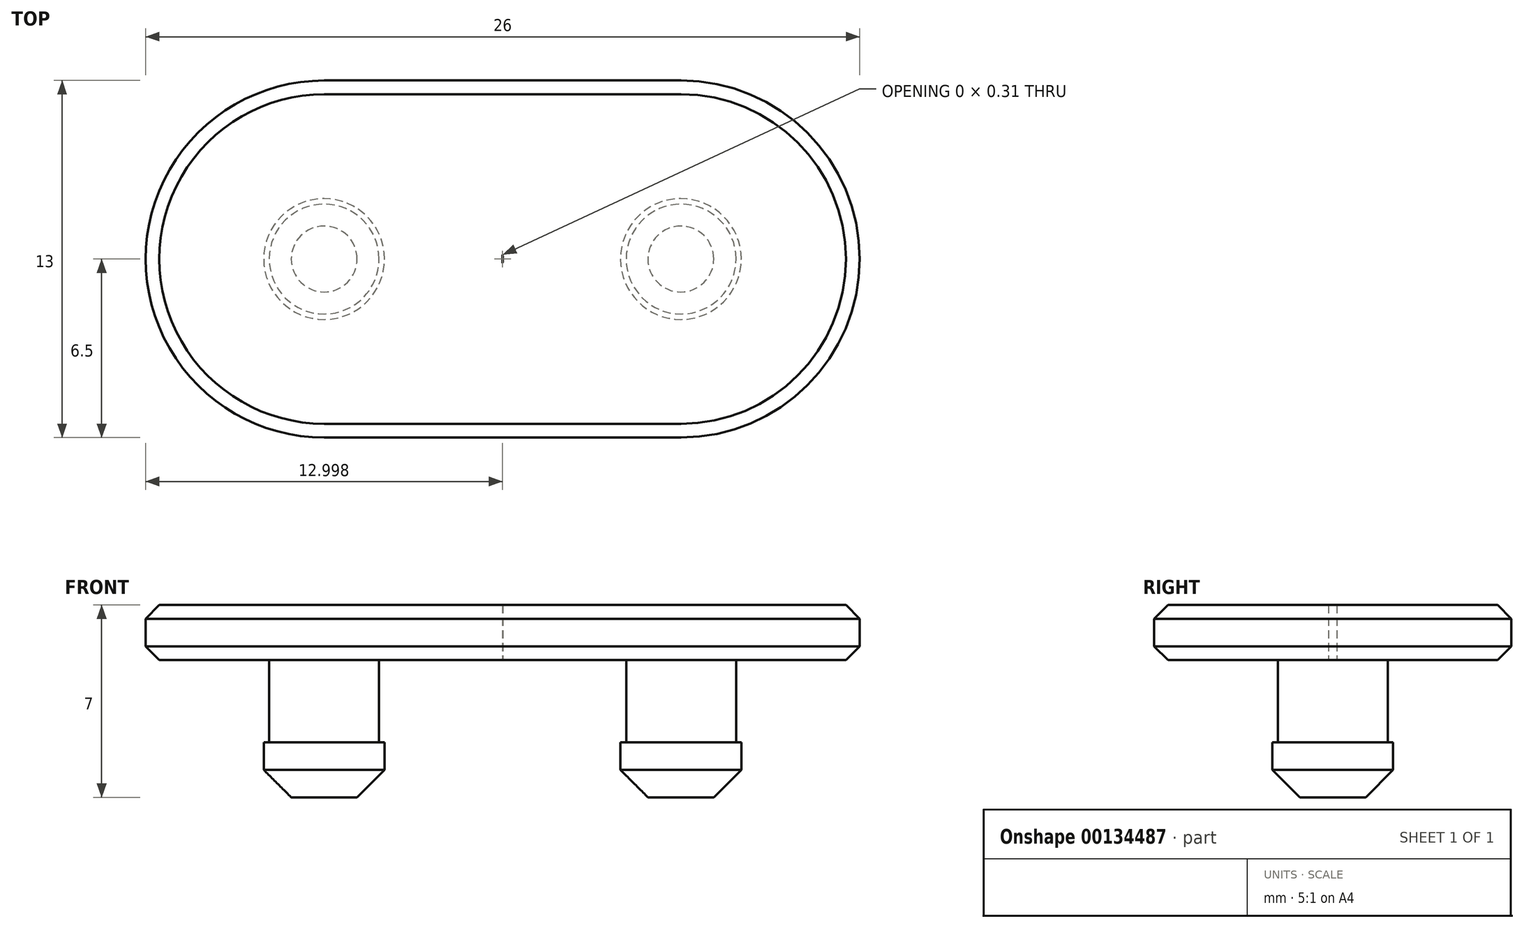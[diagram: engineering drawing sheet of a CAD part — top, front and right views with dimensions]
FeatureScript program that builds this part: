
annotation { "Feature Type Name" : "Feature", "Feature Type Description" : "" }
export const myFeature = defineFeature(function(context is Context, id is Id, definition is map)
    precondition{}
    {
        {
            var Q0;
            Q0=qCreatedBy(makeId("Top.planeOp"),FACE);
            var sketch = newSketch(context, id + "F0", { "sketchPlane" : qUnion([Q0])});
            skLineSegment(sketch, "E0.bottom", {"start": v(6.5, -6.5) * mm, "end": v(-6.5, -6.5) * mm});
            skLineSegment(sketch, "E0.top", {"start": v(6.5, 6.5) * mm, "end": v(-6.5, 6.5) * mm});
            skLineSegment(sketch, "E0.left", {"start": v(13, -0.3) * mm, "end": v(13, 0.3) * mm});
            skLineSegment(sketch, "E0.right", {"start": v(-13, -0.3) * mm, "end": v(-13, 0.3) * mm});
            skPoint(sketch, "E0.middle", {"position": v(0, 0) * mm});
            skPoint(sketch, "E1.visualSharp", {"position": v(-13, 6.5) * mm});
            skPoint(sketch, "E2.visualSharp", {"position": v(-13, -6.5) * mm});
            skPoint(sketch, "E3.visualSharp", {"position": v(13, 6.5) * mm});
            skPoint(sketch, "E4.visualSharp", {"position": v(13, -6.5) * mm});
            skLineSegment(sketch, "E5", {"start": v(0, 6.5) * mm, "end": v(0, -6.5) * mm, "construction": true});
            skLineSegment(sketch, "E6", {"start": v(0, 0) * mm, "end": v(13, 0) * mm, "construction": true});
            skCircle(sketch, "E7", {"center": v(6.5, 0) * mm, "radius": 2 * mm});
            skLineSegment(sketch, "E8", {"start": v(-13, 0) * mm, "end": v(0, 0) * mm, "construction": true});
            skCircle(sketch, "E9", {"center": v(-6.5, 0) * mm, "radius": 2 * mm});
            skCircle(sketch, "E10", {"center": v(-6.5, 0) * mm, "radius": 6.5 * mm});
            skCircle(sketch, "E11", {"center": v(6.5, 0) * mm, "radius": 6.5 * mm});
            skSolve(sketch);
        }
        {
            var Q0;
            Q0 = qSketchRegion(id + "F0", true);
            var Q1;
            Q1=makeQuery(id+"F0.imprint","IMPRINT",FACE,{"disambiguationData":[TD([[makeQuery(id+"F0.imprint","IMPRINT",EDGE,{"derivedFrom":sQuery(id+"F0.wireOp",EDGE,"E9")}),1.0]])]});
            var Q2;
            Q2=makeQuery(id+"F0.imprint","IMPRINT",FACE,{"disambiguationData":[TD([[makeQuery(id+"F0.imprint","IMPRINT",EDGE,{"derivedFrom":sQuery(id+"F0.wireOp",EDGE,"E7")}),1.0]])]});
            extrude(context, id + "F1", {"entities" : qUnion([Q0, Q1, Q2]), "depth" : 2 * mm});
        }
        {
            var Q0;
            Q0=makeQuery(id+"F0.imprint","IMPRINT",FACE,{"disambiguationData":[TD([[makeQuery(id+"F0.imprint","IMPRINT",EDGE,{"derivedFrom":sQuery(id+"F0.wireOp",EDGE,"E9")}),1.0]])]});
            var Q1;
            Q1=makeQuery(id+"F0.imprint","IMPRINT",FACE,{"disambiguationData":[TD([[makeQuery(id+"F0.imprint","IMPRINT",EDGE,{"derivedFrom":sQuery(id+"F0.wireOp",EDGE,"E7")}),1.0]])]});
            extrude(context, id + "F2", {"entities" : qUnion([Q0, Q1]), "operationType" : NewBodyOperationType.ADD, "oppositeDirection" : true, "depth" : 3 * mm});
        }
        {
            var Q0;
            Q0=makeQuery(id+"F2.opExtrude","CAP_FACE",FACE,{"disambiguationData":[OSD([sQuery(id+"F0.wireOp",EDGE,"E9")])],"isStart":false});
            var sketch = newSketch(context, id + "F3", { "sketchPlane" : qUnion([Q0])});
            skCircle(sketch, "E12", {"center": v(-6.5, 0) * mm, "radius": 2.2 * mm});
            skCircle(sketch, "E13", {"center": v(6.49, 0) * mm, "radius": 2.2 * mm});
            skSolve(sketch);
        }
        {
            var Q0;
            Q0 = qSketchRegion(id + "F3", true);
            extrude(context, id + "F4", {"entities" : qUnion([Q0]), "operationType" : NewBodyOperationType.ADD, "depth" : 2 * mm});
        }
        {
            var Q0;
            Q0=makeQuery(id+"F4.opExtrude","CAP_EDGE",EDGE,{"disambiguationData":[OSD([sQuery(id+"F3.wireOp",EDGE,"E12")])],"isStart":false});
            var Q1;
            Q1=makeQuery(id+"F4.opExtrude","CAP_EDGE",EDGE,{"disambiguationData":[OSD([sQuery(id+"F3.wireOp",EDGE,"E13")])],"isStart":false});
            chamfer(context, id + "F5", {"entities" : qUnion([Q0, Q1]), "width" : 1 * mm, "tangentPropagation" : true});
        }
        {
            var Q0;
            Q0=makeQuery(id+"F1.opExtrude","CAP_EDGE",EDGE,{"disambiguationData":[OSD([sQuery(id+"F0.wireOp",EDGE,"E0.top")])],"isStart":true});
            var Q1;
            {var subQ0=sQuery(id+"F0.wireOp",EDGE,"E10");Q1=makeQuery(id+"F1.opExtrude","CAP_EDGE",EDGE,{"disambiguationData":[OSD([subQ0]),TDD([makeQuery(id+"F0.imprint","IMPRINT",EDGE,{"disambiguationData":[TD([[makeQuery(id+"F0.imprint","INTERSECT",VERTEX,{"derivedFrom":[sQuery(id+"F0.wireOp",EDGE,"E0.bottom"),subQ0]}),1.0]])],"derivedFrom":subQ0})])],"isStart":false});}
            var Q2;
            Q2=makeQuery(id+"F1.opExtrude","CAP_EDGE",EDGE,{"disambiguationData":[OSD([sQuery(id+"F0.wireOp",EDGE,"E0.top")])],"isStart":false});
            chamfer(context, id + "F6", {"entities" : qUnion([Q0, Q1, Q2]), "width" : .5 * mm, "tangentPropagation" : true});
        }
    });
